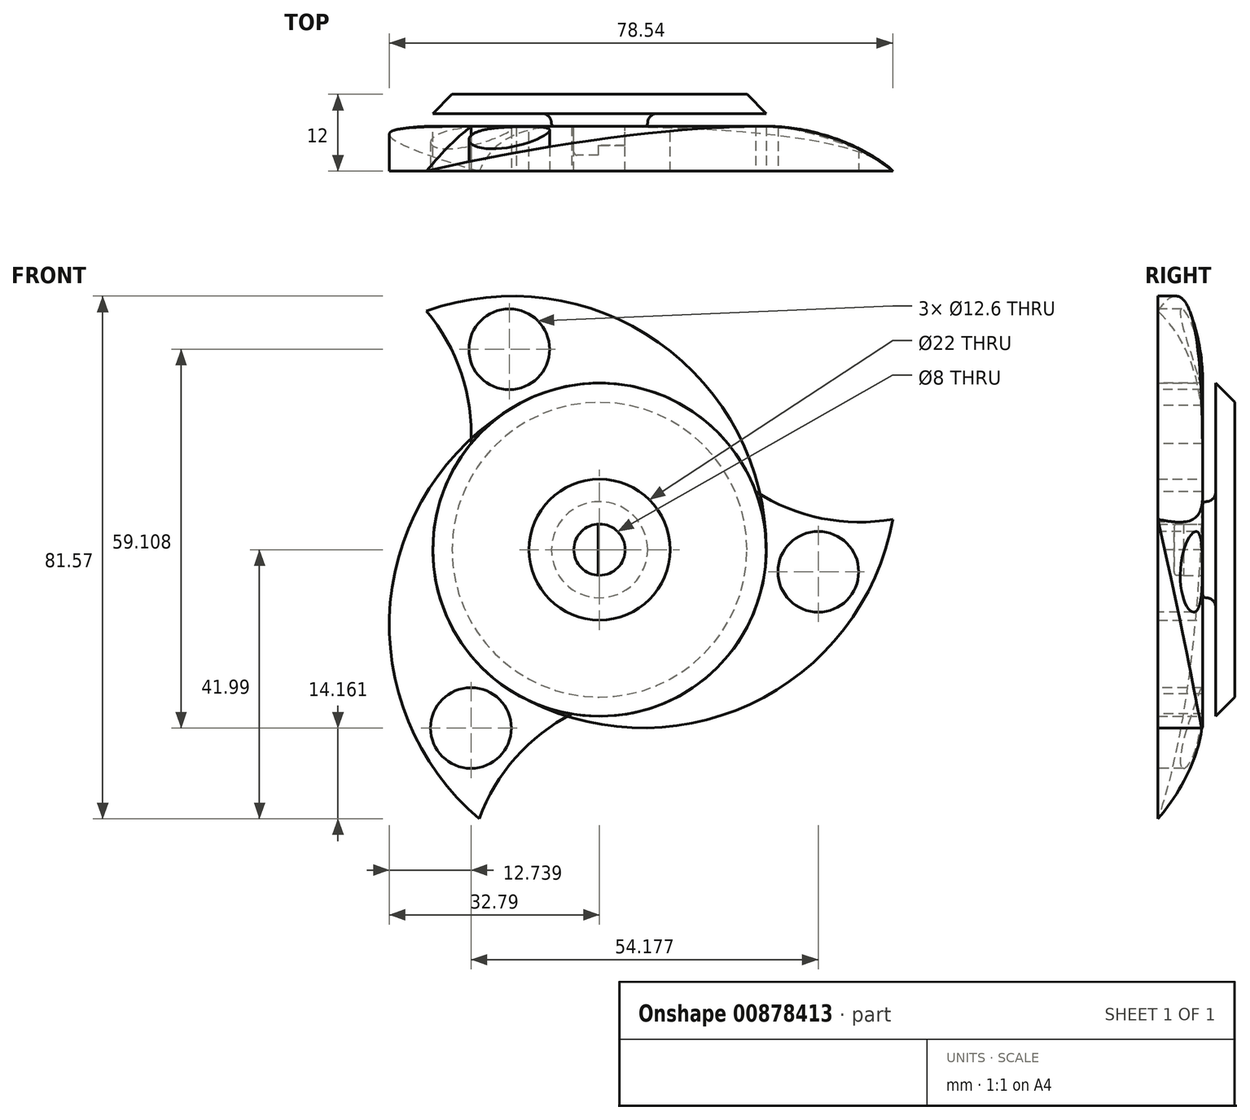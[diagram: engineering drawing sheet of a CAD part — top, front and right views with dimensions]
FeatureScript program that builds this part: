
annotation { "Feature Type Name" : "Feature", "Feature Type Description" : "" }
export const myFeature = defineFeature(function(context is Context, id is Id, definition is map)
    precondition{}
    {
        {
            var Q0;
            Q0=qCreatedBy(makeId("Top.planeOp"),FACE);
            var sketch = newSketch(context, id + "F0", { "sketchPlane" : qUnion([Q0]), "disableImprinting" : false});
            skLineSegment(sketch, "E0", {"start": v(0, 28.58) * mm, "end": v(0, -28.58) * mm, "construction": true});
            skLineSegment(sketch, "E1.bottom", {"start": v(11, 3.5) * mm, "end": v(-11, 3.5) * mm});
            skLineSegment(sketch, "E1.top", {"start": v(11, -3.5) * mm, "end": v(-11, -3.5) * mm});
            skLineSegment(sketch, "E1.left", {"start": v(11, 3.5) * mm, "end": v(11, -3.5) * mm});
            skLineSegment(sketch, "E1.right", {"start": v(-11, 3.5) * mm, "end": v(-11, -3.5) * mm});
            skPoint(sketch, "E1.middle", {"position": v(0, 0) * mm});
            skLineSegment(sketch, "E2", {"start": v(4, 3.5) * mm, "end": v(4, -3.5) * mm});
            skLineSegment(sketch, "E3.MirrorCS", {"start": v(-4, 3.5) * mm, "end": v(-4, -3.5) * mm});
            skSolve(sketch);
        }
        {
            var Q0;
            {var subQ0=sQuery(id+"F0.wireOp",EDGE,"E1.left");Q0=makeQuery(id+"F0.imprint","IMPRINT",FACE,{"disambiguationData":[TD([[makeQuery(id+"F0.imprint","IMPRINT",EDGE,{"derivedFrom":subQ0}),-1.0]])]});}
            var Q1;
            Q1=sQuery(id+"F0.wireOp",EDGE,"E0");
            revolve(context, id + "F1", {"surfaceOperationType" : NewSurfaceOperationType.NEW, "entities" : qUnion([Q0]), "axis" : qUnion([Q1]), "revolveType" : RevolveType.FULL});
        }
        {
            var Q0;
            Q0=makeQuery(id+"F1.opRevolve","SWEPT_FACE",FACE,{"disambiguationData":[OSD([sQuery(id+"F0.wireOp",EDGE,"E1.top")])]});
            cPlane(context, id + "F2", {"entities" : qUnion([Q0]), "cplaneType" : CPlaneType.OFFSET, "offset" : 0 * mm, "width" : 150 * mm, "height" : 150 * mm});
        }
        {
            var Q0;
            Q0=qCreatedBy(makeId("Top.planeOp"),FACE);
            var sketch = newSketch(context, id + "F3", { "sketchPlane" : qUnion([Q0])});
            skLineSegment(sketch, "E4.bottom", {"start": v(11, 3.5) * mm, "end": v(26, 3.5) * mm});
            skLineSegment(sketch, "E4.top", {"start": v(11, -3.5) * mm, "end": v(26, -3.5) * mm});
            skLineSegment(sketch, "E4.left", {"start": v(11, 3.5) * mm, "end": v(11, -3.5) * mm});
            skLineSegment(sketch, "E4.right", {"start": v(26, 3.5) * mm, "end": v(26, -3.5) * mm});
            skSolve(sketch);
        }
        {
            var Q0;
            Q0=makeQuery(id+"F3.imprint","IMPRINT",FACE,{"disambiguationData":[TD([[makeQuery(id+"F3.imprint","IMPRINT",EDGE,{"derivedFrom":sQuery(id+"F3.wireOp",EDGE,"E4.bottom")}),-1.0]])]});
            var Q1;
            Q1 = qSketchRegion(id + "F5", true);
            var Q2;
            Q2=sQuery(id+"F0.wireOp",EDGE,"E0");
            revolve(context, id + "F4", {"surfaceOperationType" : NewSurfaceOperationType.NEW, "entities" : qUnion([Q0, Q1]), "axis" : qUnion([Q2]), "revolveType" : RevolveType.FULL});
        }
        {
            var Q0;
            Q0=qCreatedBy(id+"F2.planeOp",FACE);
            var sketch = newSketch(context, id + "F5", { "sketchPlane" : qUnion([Q0]), "disableImprinting" : false});
            skCircle(sketch, "E5", {"center": v(0, 0) * mm, "radius": 46 * mm, "construction": true});
            skCircle(sketch, "E6", {"center": v(0, 0) * mm, "radius": 26 * mm});
            skCircle(sketch, "E7", {"center": v(-13.58, 0) * mm, "radius": 39.58 * mm});
            skCircle(sketch, "E8", {"center": v(-50, 18) * mm, "radius": 30 * mm});
            skCircle(sketch, "E9", {"center": v(-14.08, 31.28) * mm, "radius": 6.3 * mm});
            skCircle(sketch, "E10", {"center": v(-14.08, 31.28) * mm, "radius": 8.3 * mm, "construction": true});
            skPoint(sketch, "E11", {"position": v(-26.99, 37.24) * mm});
            skLineSegment(sketch, "E12", {"start": v(0, 0) * mm, "end": v(46, 0) * mm, "construction": true});
            skSolve(sketch);
        }
        {
            var Q0;
            Q0=makeQuery(id+"F5.imprint","IMPRINT",FACE,{"disambiguationData":[TD([[makeQuery(id+"F5.imprint","IMPRINT",EDGE,{"derivedFrom":sQuery(id+"F5.wireOp",EDGE,"E9")}),-1.0]])]});
            var Q1;
            Q1 = qSketchRegion(id + "F12", true);
            extrude(context, id + "F6", {"entities" : qUnion([Q0, Q1]), "oppositeDirection" : true, "depth" : 7 * mm, "offsetDistance" : 25 * mm});
        }
        {
            var Q0;
            Q0=makeQuery(id+"F6.opExtrude","SWEPT_BODY",BODY,{"disambiguationData":[OSD([sQuery(id+"F5.wireOp",EDGE,"E6"),sQuery(id+"F5.wireOp",EDGE,"E7"),sQuery(id+"F5.wireOp",EDGE,"E8"),sQuery(id+"F5.wireOp",EDGE,"E9")])]});
            var Q1;
            Q1=sQuery(id+"F0.wireOp",EDGE,"E0");
            circularPattern(context, id + "F7", {"entities" : qUnion([Q0]), "axis" : qUnion([Q1]), "angle" : 360 * degree, "instanceCount" : 3, "equalSpace" : true, "fullFeaturePattern" : false, "computeTransformsWithoutBuiltin" : true});
        }
        {
            var Q0;
            Q0=qCreatedBy(makeId("Top.planeOp"),FACE);
            var sketch = newSketch(context, id + "F8", { "sketchPlane" : qUnion([Q0]), "disableImprinting" : false});
            skLineSegment(sketch, "E13", {"start": v(46, -3.5) * mm, "end": v(26, -3.5) * mm});
            skLineSegment(sketch, "E14", {"start": v(26, -3.5) * mm, "end": v(26, 3.5) * mm});
            skLineSegment(sketch, "E15", {"start": v(26, 3.5) * mm, "end": v(46, 3.5) * mm, "construction": true});
            skLineSegment(sketch, "E16", {"start": v(46, 3.5) * mm, "end": v(46, -3.5) * mm, "construction": true});
            skArc(sketch, "E17", {"start": v(46, -3.5) * mm, "mid": v(36.6, 1.7) * mm, "end": v(26, 3.5) * mm});
            skLineSegment(sketch, "E18", {"start": v(26, 3.5) * mm, "end": v(26, 5) * mm});
            skLineSegment(sketch, "E19", {"start": v(26, 5) * mm, "end": v(48, 5) * mm});
            skLineSegment(sketch, "E20", {"start": v(48, 5) * mm, "end": v(48, -5) * mm});
            skLineSegment(sketch, "E21", {"start": v(48, -5) * mm, "end": v(26, -5) * mm});
            skLineSegment(sketch, "E22", {"start": v(26, -5) * mm, "end": v(26, -3.5) * mm});
            skSolve(sketch);
        }
        {
            var Q0;
            Q0=makeQuery(id+"F8.imprint","IMPRINT",FACE,{"disambiguationData":[TD([[makeQuery(id+"F8.imprint","IMPRINT",EDGE,{"derivedFrom":sQuery(id+"F8.wireOp",EDGE,"E13")}),1.0]])]});
            var Q1;
            Q1=sQuery(id+"F0.wireOp",EDGE,"E0");
            revolve(context, id + "F9", {"operationType" : NewBodyOperationType.REMOVE, "surfaceOperationType" : NewSurfaceOperationType.NEW, "entities" : qUnion([Q0]), "axis" : qUnion([Q1]), "revolveType" : RevolveType.FULL, "oppositeDirection" : true});
        }
        {
            var Q0;
            Q0=qCreatedBy(makeId("Top.planeOp"),FACE);
            var sketch = newSketch(context, id + "F10", { "sketchPlane" : qUnion([Q0])});
            skLineSegment(sketch, "E23", {"start": v(26, 5.5) * mm, "end": v(26, 8.5) * mm});
            skLineSegment(sketch, "E24", {"start": v(26, 8.5) * mm, "end": v(0, 8.5) * mm});
            skLineSegment(sketch, "E25", {"start": v(0, 8.5) * mm, "end": v(0, -1) * mm});
            skLineSegment(sketch, "E26", {"start": v(0, -1) * mm, "end": v(4, -1) * mm});
            skLineSegment(sketch, "E27", {"start": v(4, -1) * mm, "end": v(4, 3.5) * mm});
            skLineSegment(sketch, "E28", {"start": v(4, 3.5) * mm, "end": v(7, 3.5) * mm});
            skLineSegment(sketch, "E29", {"start": v(7.5, 4) * mm, "end": v(7.5, 4) * mm});
            skLineSegment(sketch, "E30", {"start": v(9, 5.5) * mm, "end": v(26, 5.5) * mm});
            skPoint(sketch, "E31.visualSharp", {"position": v(7.5, 5.5) * mm});
            skArc(sketch, "E31.filletArc", {"start": v(9, 5.5) * mm, "mid": v(7.94, 5.06) * mm, "end": v(7.5, 4) * mm});
            skPoint(sketch, "E32.visualSharp", {"position": v(7.5, 3.5) * mm});
            skArc(sketch, "E32.filletArc", {"start": v(7, 3.5) * mm, "mid": v(7.35, 3.65) * mm, "end": v(7.5, 4) * mm});
            skLineSegment(sketch, "E33", {"start": v(26, 10) * mm, "end": v(26, 5) * mm, "construction": true});
            skSolve(sketch);
        }
        {
            var Q0;
            Q0=makeQuery(id+"F10.imprint","IMPRINT",FACE,{"disambiguationData":[TD([[makeQuery(id+"F10.imprint","IMPRINT",EDGE,{"derivedFrom":sQuery(id+"F10.wireOp",EDGE,"E23")}),1.0]])]});
            var Q1;
            Q1=sQuery(id+"F0.wireOp",EDGE,"E0");
            revolve(context, id + "F11", {"surfaceOperationType" : NewSurfaceOperationType.NEW, "entities" : qUnion([Q0]), "axis" : qUnion([Q1]), "revolveType" : RevolveType.FULL});
        }
        {
            var Q0;
            Q0=makeQuery(id+"F11.opRevolve","SWEPT_FACE",FACE,{"disambiguationData":[OSD([sQuery(id+"F10.wireOp",EDGE,"E26")])]});
            var sketch = newSketch(context, id + "F12", { "sketchPlane" : qUnion([Q0])});
            skLineSegment(sketch, "E34.bottom", {"start": v(-0.2, 4.5) * mm, "end": v(4.8, 4.5) * mm});
            skLineSegment(sketch, "E34.top", {"start": v(-0.2, -4.5) * mm, "end": v(4.8, -4.5) * mm});
            skLineSegment(sketch, "E34.left", {"start": v(-0.2, 4.5) * mm, "end": v(-0.2, -4.5) * mm});
            skLineSegment(sketch, "E34.right", {"start": v(4.8, 4.5) * mm, "end": v(4.8, -4.5) * mm});
            skSolve(sketch);
        }
        {
            var Q0;
            {var subQ0=sQuery(id+"F12.wireOp",EDGE,"E34.left");var subQ1=makeQuery(id+"F11.opRevolve","SWEPT_EDGE",EDGE,{"disambiguationData":[OSD([sQuery(id+"F10.wireOp",EDGE,"E26"),sQuery(id+"F10.wireOp",EDGE,"E27")])]});var subQ2=makeQuery(id+"F12.imprint","INTERSECT",VERTEX,{"disambiguationData":[OD(0.0)],"derivedFrom":[subQ1,subQ0]});Q0=makeQuery(id+"F12.imprint","IMPRINT",FACE,{"disambiguationData":[TD([[makeQuery(id+"F12.imprint","IMPRINT",EDGE,{"disambiguationData":[TD([[subQ2,-1.0]])],"derivedFrom":subQ0}),1.0]])]});}
            extrude(context, id + "F13", {"entities" : qUnion([Q0]), "operationType" : NewBodyOperationType.REMOVE, "oppositeDirection" : true, "depth" : 1.5 * mm, "offsetDistance" : 25 * mm});
        }
        {
            var Q0;
            Q0=makeQuery(id+"F11.opRevolve","SWEPT_EDGE",EDGE,{"disambiguationData":[OSD([sQuery(id+"F10.wireOp",EDGE,"E26"),sQuery(id+"F10.wireOp",EDGE,"E27")])]});
            var Q1;
            Q1=makeQuery(id+"F13.boolean.opBoolean","COPY",EDGE,{"derivedFrom":makeQuery(id+"F13.opExtrude","CAP_EDGE",EDGE,{"disambiguationData":[OSD([sQuery(id+"F12.wireOp",EDGE,"E34.left")])],"isStart":true})});
            var Q2;
            Q2=makeQuery(id+"F13.boolean.opBoolean","COPY",EDGE,{"derivedFrom":makeQuery(id+"F13.opExtrude","CAP_EDGE",EDGE,{"disambiguationData":[OSD([sQuery(id+"F10.wireOp",EDGE,"E26"),sQuery(id+"F10.wireOp",EDGE,"E27")])],"isStart":false})});
            fillet(context, id + "F14", {"entities" : qUnion([Q0, Q1, Q2]), "radius" : .5 * mm, "tangentPropagation" : true, "defaultsChanged" : false, "vertexSettings" : [], "allowEdgeOverflow" : false});
        }
        {
            var Q0;
            Q0=makeQuery(id+"F11.opRevolve","SWEPT_EDGE",EDGE,{"disambiguationData":[OSD([sQuery(id+"F10.wireOp",EDGE,"E23"),sQuery(id+"F10.wireOp",EDGE,"E24")])]});
            chamfer(context, id + "F15", {"entities" : qUnion([Q0]), "width" : 3 * mm, "tangentPropagation" : true});
        }
    });
